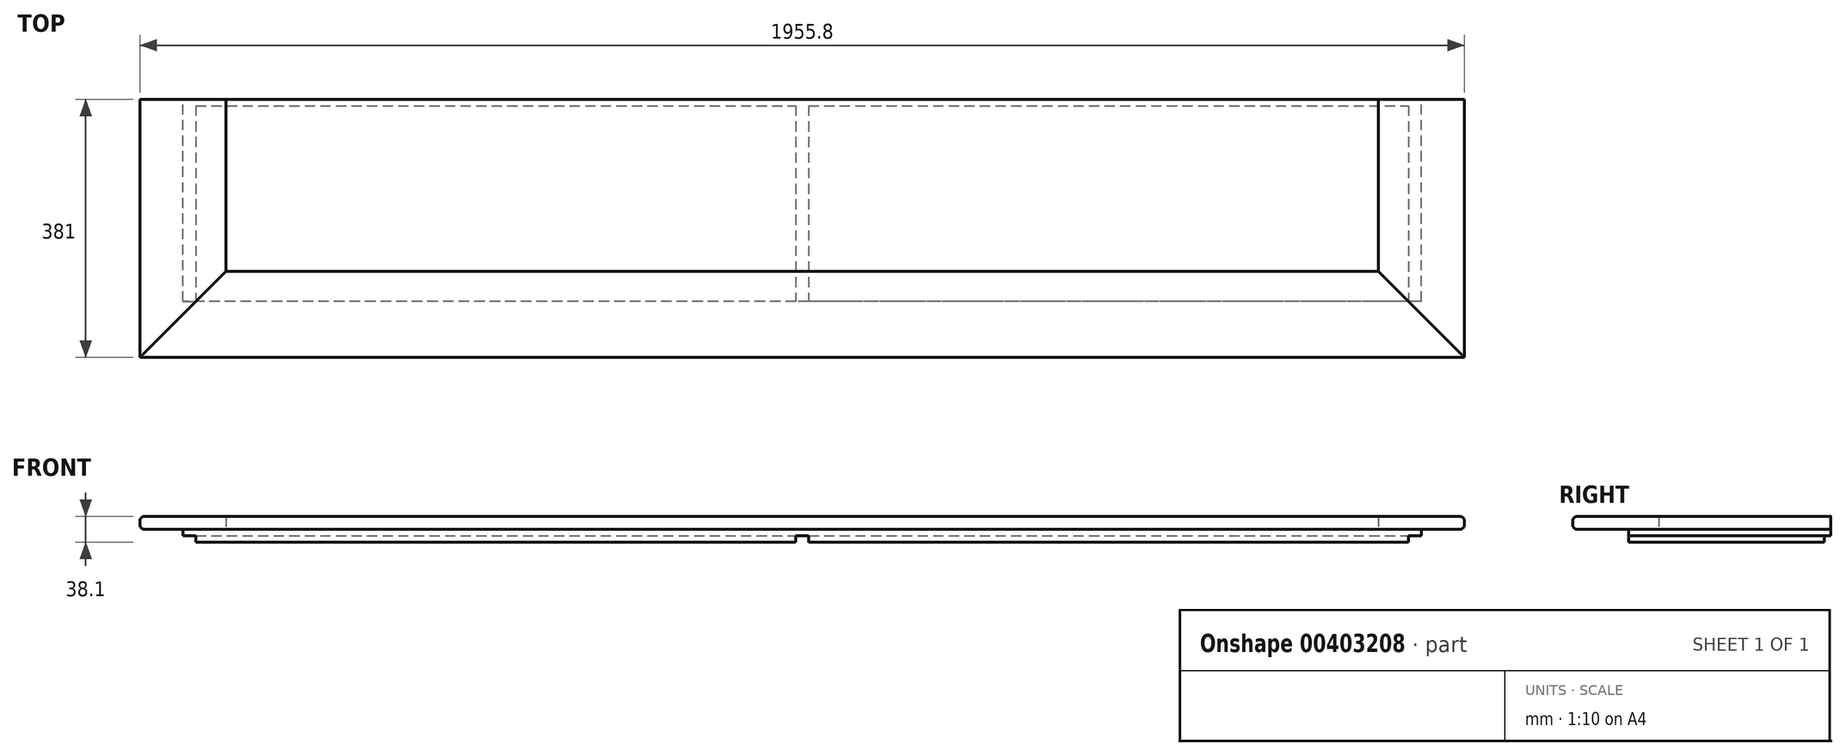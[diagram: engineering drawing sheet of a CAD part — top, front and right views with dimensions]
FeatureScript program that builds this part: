
annotation { "Feature Type Name" : "Feature", "Feature Type Description" : "" }
export const myFeature = defineFeature(function(context is Context, id is Id, definition is map)
    precondition{}
    {
        {
            var Q0;
            Q0=qCreatedBy(makeId("Top.planeOp"),FACE);
            var sketch = newSketch(context, id + "F0", { "sketchPlane" : qUnion([Q0])});
            skLineSegment(sketch, "E0.bottom", {"start": v(914.4, -149.22) * mm, "end": v(-914.4, -149.23) * mm});
            skLineSegment(sketch, "E0.top", {"start": v(914.4, 149.23) * mm, "end": v(-914.4, 149.22) * mm});
            skLineSegment(sketch, "E0.left", {"start": v(914.4, -149.22) * mm, "end": v(914.4, 149.23) * mm});
            skLineSegment(sketch, "E0.right", {"start": v(-914.4, -149.23) * mm, "end": v(-914.4, 149.22) * mm});
            skPoint(sketch, "E0.middle", {"position": v(0, 0) * mm});
            skSolve(sketch);
        }
        {
            var Q0;
            Q0=qSketchRegion(id+"F0",true);
            extrude(context, id + "F1", {"entities" : qUnion([Q0]), "depth" : 19.05 * mm});
        }
        {
            var Q0;
            Q0=makeQuery(id+"F1.opExtrude","SWEPT_FACE",FACE,{"disambiguationData":[OSD([sQuery(id+"F0.wireOp",EDGE,"E0.left")])]});
            var sketch = newSketch(context, id + "F2", { "sketchPlane" : qUnion([Q0])});
            skLineSegment(sketch, "E1.bottom", {"start": v(149.23, 9.53) * mm, "end": v(139.7, 9.53) * mm});
            skLineSegment(sketch, "E1.top", {"start": v(149.23, 0) * mm, "end": v(139.7, 0) * mm});
            skLineSegment(sketch, "E1.left", {"start": v(149.23, 9.53) * mm, "end": v(149.23, 0) * mm});
            skLineSegment(sketch, "E1.right", {"start": v(139.7, 9.53) * mm, "end": v(139.7, 0) * mm});
            skSolve(sketch);
        }
        {
            var Q0;
            Q0=qSketchRegion(id+"F2",true);
            extrude(context, id + "F3", {"entities" : qUnion([Q0]), "operationType" : NewBodyOperationType.REMOVE, "endBound" : BoundingType.THROUGH_ALL, "oppositeDirection" : true, "depth" : 25.4 * mm});
        }
        {
            var Q0;
            Q0=makeQuery(id+"F1.opExtrude","SWEPT_FACE",FACE,{"disambiguationData":[OSD([sQuery(id+"F0.wireOp",EDGE,"E0.bottom")])]});
            var sketch = newSketch(context, id + "F4", { "sketchPlane" : qUnion([Q0])});
            skLineSegment(sketch, "E2.bottom", {"start": v(-914.4, 9.53) * mm, "end": v(-895.35, 9.53) * mm});
            skLineSegment(sketch, "E2.top", {"start": v(-914.4, 0) * mm, "end": v(-895.35, 0) * mm});
            skLineSegment(sketch, "E2.left", {"start": v(-914.4, 9.53) * mm, "end": v(-914.4, 0) * mm});
            skLineSegment(sketch, "E2.right", {"start": v(-895.35, 9.53) * mm, "end": v(-895.35, 0) * mm});
            skLineSegment(sketch, "E3", {"start": v(0, 19.05) * mm, "end": v(0, 0) * mm, "construction": true});
            skLineSegment(sketch, "E4.MirrorCS", {"start": v(895.35, 9.53) * mm, "end": v(895.35, 0) * mm});
            skLineSegment(sketch, "E5.MirrorCS", {"start": v(914.4, 9.53) * mm, "end": v(914.4, 0) * mm});
            skLineSegment(sketch, "E6.MirrorCS", {"start": v(914.4, 0) * mm, "end": v(895.35, 0) * mm});
            skLineSegment(sketch, "E7.MirrorCS", {"start": v(914.4, 9.53) * mm, "end": v(895.35, 9.53) * mm});
            skLineSegment(sketch, "E8", {"start": v(-452.44, 0) * mm, "end": v(-452.44, 19.05) * mm, "construction": true});
            skLineSegment(sketch, "E9.MirrorCS", {"start": v(9.53, 9.53) * mm, "end": v(-9.53, 9.53) * mm});
            skLineSegment(sketch, "E10.MirrorCS", {"start": v(9.53, 9.53) * mm, "end": v(9.53, 0) * mm});
            skLineSegment(sketch, "E11.MirrorCS", {"start": v(9.53, 0) * mm, "end": v(-9.53, 0) * mm});
            skLineSegment(sketch, "E12.MirrorCS", {"start": v(-9.53, 9.53) * mm, "end": v(-9.53, 0) * mm});
            skSolve(sketch);
        }
        {
            var Q0;
            Q0=qSketchRegion(id+"F4",true);
            extrude(context, id + "F5", {"entities" : qUnion([Q0]), "operationType" : NewBodyOperationType.REMOVE, "endBound" : BoundingType.THROUGH_ALL, "oppositeDirection" : true, "depth" : 25.4 * mm});
        }
        {
            var Q0;
            Q0=makeQuery(id+"F1.opExtrude","CAP_FACE",FACE,{"disambiguationData":[OSD([sQuery(id+"F0.wireOp",EDGE,"E0.bottom"),sQuery(id+"F0.wireOp",EDGE,"E0.top"),sQuery(id+"F0.wireOp",EDGE,"E0.left"),sQuery(id+"F0.wireOp",EDGE,"E0.right")])],"isStart":false});
            var sketch = newSketch(context, id + "F6", { "sketchPlane" : qUnion([Q0])});
            skLineSegment(sketch, "E13.bottom", {"start": v(-850.9, -104.78) * mm, "end": v(850.9, -104.77) * mm});
            skLineSegment(sketch, "E13.top", {"start": v(-977.9, -231.78) * mm, "end": v(977.9, -231.77) * mm});
            skLineSegment(sketch, "E14", {"start": v(-977.9, -231.78) * mm, "end": v(-850.9, -104.78) * mm});
            skLineSegment(sketch, "E15", {"start": v(977.9, -231.77) * mm, "end": v(850.9, -104.77) * mm});
            skSolve(sketch);
        }
        {
            var Q0;
            Q0=qSketchRegion(id+"F6",true);
            extrude(context, id + "F7", {"entities" : qUnion([Q0]), "depth" : 19.05 * mm});
        }
        {
            var Q0;
            Q0=makeQuery(id+"F1.opExtrude","CAP_FACE",FACE,{"disambiguationData":[OSD([sQuery(id+"F0.wireOp",EDGE,"E0.bottom"),sQuery(id+"F0.wireOp",EDGE,"E0.top"),sQuery(id+"F0.wireOp",EDGE,"E0.left"),sQuery(id+"F0.wireOp",EDGE,"E0.right")])],"isStart":false});
            var sketch = newSketch(context, id + "F8", { "sketchPlane" : qUnion([Q0])});
            skLineSegment(sketch, "E16.bottom", {"start": v(-977.9, 149.22) * mm, "end": v(-850.9, 149.22) * mm});
            skLineSegment(sketch, "E16.left", {"start": v(-977.9, 149.22) * mm, "end": v(-977.9, -231.78) * mm});
            skLineSegment(sketch, "E16.right", {"start": v(-850.9, 149.22) * mm, "end": v(-850.9, -104.78) * mm});
            skLineSegment(sketch, "E17", {"start": v(-977.9, -231.78) * mm, "end": v(-850.9, -104.78) * mm});
            skSolve(sketch);
        }
        {
            var Q0;
            Q0=qSketchRegion(id+"F8",true);
            extrude(context, id + "F9", {"entities" : qUnion([Q0]), "depth" : 19.05 * mm});
        }
        {
            var Q0;
            Q0=makeQuery(id+"F1.opExtrude","CAP_FACE",FACE,{"disambiguationData":[OSD([sQuery(id+"F0.wireOp",EDGE,"E0.bottom"),sQuery(id+"F0.wireOp",EDGE,"E0.top"),sQuery(id+"F0.wireOp",EDGE,"E0.left"),sQuery(id+"F0.wireOp",EDGE,"E0.right")])],"isStart":false});
            var sketch = newSketch(context, id + "F10", { "sketchPlane" : qUnion([Q0])});
            skLineSegment(sketch, "E18.bottom", {"start": v(850.9, 149.23) * mm, "end": v(977.9, 149.23) * mm});
            skLineSegment(sketch, "E18.left", {"start": v(850.9, 149.23) * mm, "end": v(850.9, -104.78) * mm});
            skLineSegment(sketch, "E18.right", {"start": v(977.9, 149.23) * mm, "end": v(977.9, -231.77) * mm});
            skLineSegment(sketch, "E19", {"start": v(977.9, -231.77) * mm, "end": v(850.9, -104.78) * mm});
            skSolve(sketch);
        }
        {
            var Q0;
            Q0=qSketchRegion(id+"F10",true);
            extrude(context, id + "F11", {"entities" : qUnion([Q0]), "depth" : 19.05 * mm});
        }
        {
            var Q0;
            Q0=makeQuery(id+"F7.opExtrude","CAP_EDGE",EDGE,{"disambiguationData":[OSD([sQuery(id+"F6.wireOp",EDGE,"E13.top")])],"isStart":false});
            var Q1;
            Q1=makeQuery(id+"F7.opExtrude","CAP_EDGE",EDGE,{"disambiguationData":[OSD([sQuery(id+"F6.wireOp",EDGE,"E13.top")])],"isStart":true});
            var Q2;
            Q2=makeQuery(id+"F11.opExtrude","CAP_EDGE",EDGE,{"disambiguationData":[OSD([sQuery(id+"F10.wireOp",EDGE,"E18.right")])],"isStart":true});
            var Q3;
            Q3=makeQuery(id+"F11.opExtrude","CAP_EDGE",EDGE,{"disambiguationData":[OSD([sQuery(id+"F10.wireOp",EDGE,"E18.right")])],"isStart":false});
            var Q4;
            Q4=makeQuery(id+"F9.opExtrude","CAP_EDGE",EDGE,{"disambiguationData":[OSD([sQuery(id+"F8.wireOp",EDGE,"E16.left")])],"isStart":false});
            var Q5;
            Q5=makeQuery(id+"F9.opExtrude","CAP_EDGE",EDGE,{"disambiguationData":[OSD([sQuery(id+"F8.wireOp",EDGE,"E16.left")])],"isStart":true});
            fillet(context, id + "F12", {"entities" : qUnion([Q0, Q1, Q2, Q3, Q4, Q5]), "radius" : 6.35 * mm, "tangentPropagation" : true, "allowEdgeOverflow" : false});
        }
        {
            var Q0;
            Q0=makeQuery(id+"F1.opExtrude","CAP_EDGE",EDGE,{"disambiguationData":[OSD([sQuery(id+"F0.wireOp",EDGE,"E0.right")])],"isStart":false});
            var Q1;
            Q1=makeQuery(id+"F1.opExtrude","CAP_EDGE",EDGE,{"disambiguationData":[OSD([sQuery(id+"F0.wireOp",EDGE,"E0.left")])],"isStart":false});
            fillet(context, id + "F13", {"entities" : qUnion([Q0, Q1]), "radius" : 3.17 * mm, "tangentPropagation" : true, "allowEdgeOverflow" : false});
        }
    });
